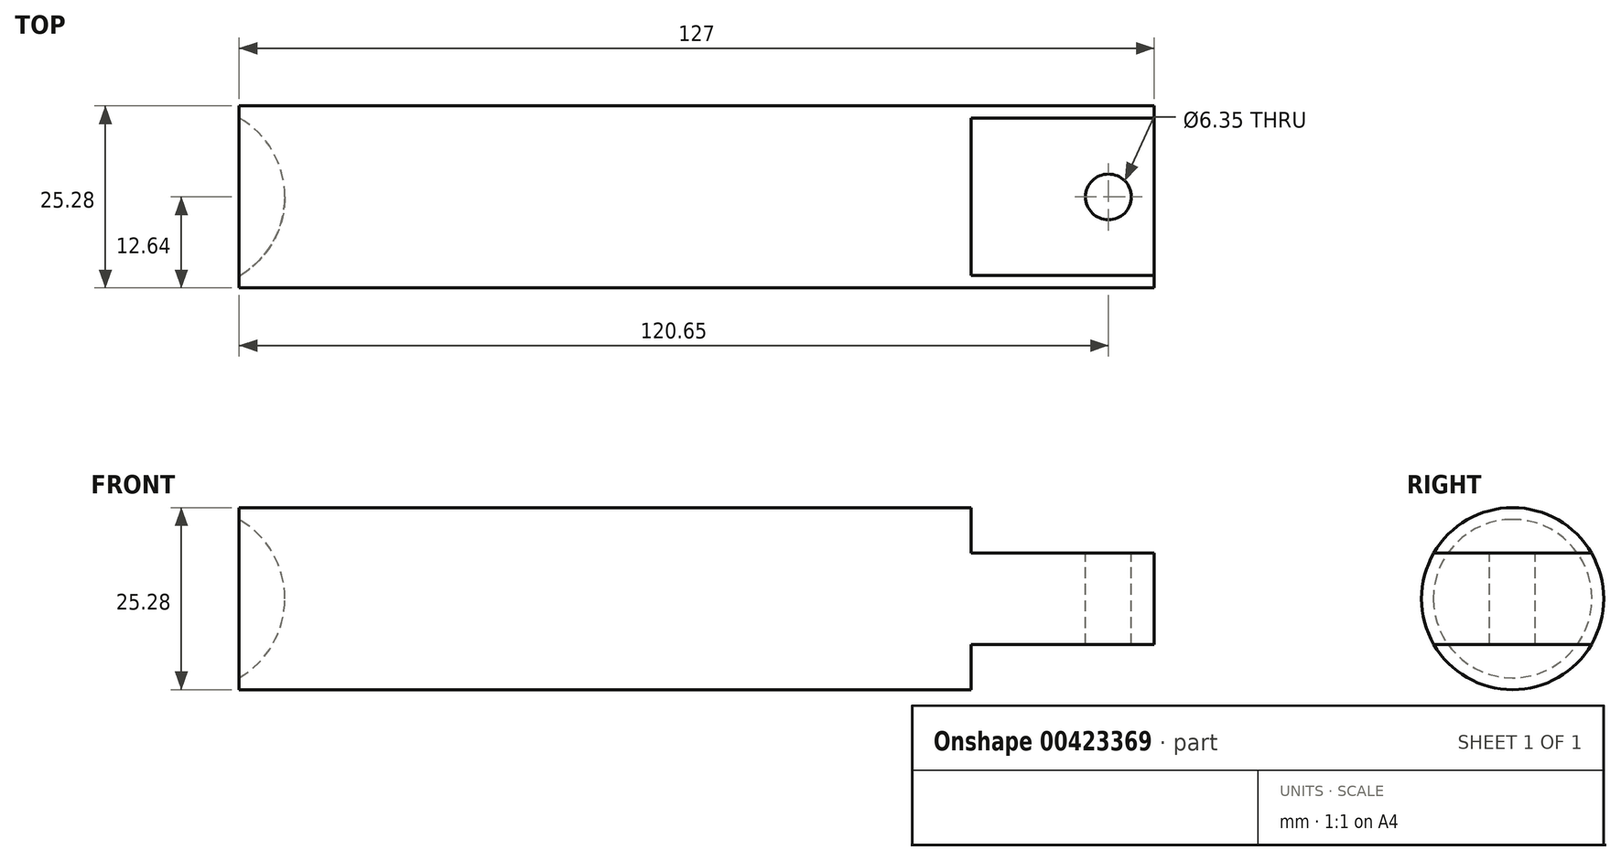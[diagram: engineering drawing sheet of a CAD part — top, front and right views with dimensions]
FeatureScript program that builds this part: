
annotation { "Feature Type Name" : "Feature", "Feature Type Description" : "" }
export const myFeature = defineFeature(function(context is Context, id is Id, definition is map)
    precondition{}
    {
        {
            var Q0;
            Q0=qCreatedBy(makeId("Right.planeOp"),FACE);
            var sketch = newSketch(context, id + "F0", { "sketchPlane" : qUnion([Q0])});
            skCircle(sketch, "E0", {"center": v(0, 0) * mm, "radius": 12.64 * mm});
            skSolve(sketch);
        }
        {
            var Q0;
            Q0 = qSketchRegion(id + "F0", true);
            extrude(context, id + "F1", {"entities" : qUnion([Q0]), "endBound" : BoundingType.SYMMETRIC, "depth" : 127 * mm});
        }
        {
            var Q0;
            Q0=qCreatedBy(makeId("Front.planeOp"),FACE);
            var sketch = newSketch(context, id + "F2", { "sketchPlane" : qUnion([Q0])});
            skLineSegment(sketch, "E1.bottom", {"start": v(69.83, 6.35) * mm, "end": v(38.1, 6.35) * mm});
            skLineSegment(sketch, "E1.top", {"start": v(69.83, 22.3) * mm, "end": v(38.1, 22.3) * mm});
            skLineSegment(sketch, "E1.left", {"start": v(69.83, 6.35) * mm, "end": v(69.83, 22.3) * mm});
            skLineSegment(sketch, "E1.right", {"start": v(38.1, 6.35) * mm, "end": v(38.1, 22.3) * mm});
            skLineSegment(sketch, "E2.bottom", {"start": v(69.83, -6.35) * mm, "end": v(38.1, -6.35) * mm});
            skLineSegment(sketch, "E2.top", {"start": v(69.83, -17.87) * mm, "end": v(38.1, -17.87) * mm});
            skLineSegment(sketch, "E2.left", {"start": v(69.83, -6.35) * mm, "end": v(69.83, -17.87) * mm});
            skLineSegment(sketch, "E2.right", {"start": v(38.1, -6.35) * mm, "end": v(38.1, -17.87) * mm});
            skSolve(sketch);
        }
        {
            var Q0;
            Q0 = qSketchRegion(id + "F2", true);
            extrude(context, id + "F3", {"entities" : qUnion([Q0]), "operationType" : NewBodyOperationType.REMOVE, "endBound" : BoundingType.SYMMETRIC, "oppositeDirection" : true, "depth" : 508 * mm});
        }
        {
            var Q0;
            Q0=makeQuery(id+"F3.boolean.opBoolean","COPY",FACE,{"derivedFrom":makeQuery(id+"F3.opExtrude","SWEPT_FACE",FACE,{"disambiguationData":[OSD([sQuery(id+"F2.wireOp",EDGE,"E1.bottom")])]})});
            var sketch = newSketch(context, id + "F4", { "sketchPlane" : qUnion([Q0])});
            skCircle(sketch, "E3", {"center": v(57.15, 0) * mm, "radius": 3.18 * mm});
            skSolve(sketch);
        }
        {
            var Q0;
            Q0 = qSketchRegion(id + "F4", true);
            extrude(context, id + "F5", {"entities" : qUnion([Q0]), "operationType" : NewBodyOperationType.REMOVE, "oppositeDirection" : true, "depth" : 25.4 * mm});
        }
        {
            var Q0;
            Q0=qCreatedBy(makeId("Top.planeOp"),FACE);
            var sketch = newSketch(context, id + "F6", { "sketchPlane" : qUnion([Q0])});
            skLineSegment(sketch, "E4.0", {"start": v(-63.5, 11) * mm, "end": v(-63.5, -11) * mm});
            skArc(sketch, "E5", {"start": v(-57.15, 0) * mm, "mid": v(-58.85, 6.35) * mm, "end": v(-63.5, 11) * mm});
            skLineSegment(sketch, "E6", {"start": v(-63.5, 0) * mm, "end": v(-57.15, 0) * mm});
            skLineSegment(sketch, "E7", {"start": v(-57.15, 0) * mm, "end": v(-63.5, 0) * mm});
            skLineSegment(sketch, "E8", {"start": v(-63.5, 11) * mm, "end": v(-63.5, 0) * mm});
            skPoint(sketch, "E9.orphan", {"position": v(-63.5, 12.64) * mm});
            skPoint(sketch, "E10.orphan", {"position": v(-63.5, -12.64) * mm});
            skSolve(sketch);
        }
        {
            var Q0;
            Q0 = qSketchRegion(id + "F6", true);
            var Q1;
            Q1=sQuery(id+"F6.wireOp",EDGE,"E7");
            revolve(context, id + "F7", {"operationType" : NewBodyOperationType.REMOVE, "entities" : qUnion([Q0]), "axis" : qUnion([Q1]), "revolveType" : RevolveType.FULL, "oppositeDirection" : true});
        }
    });
